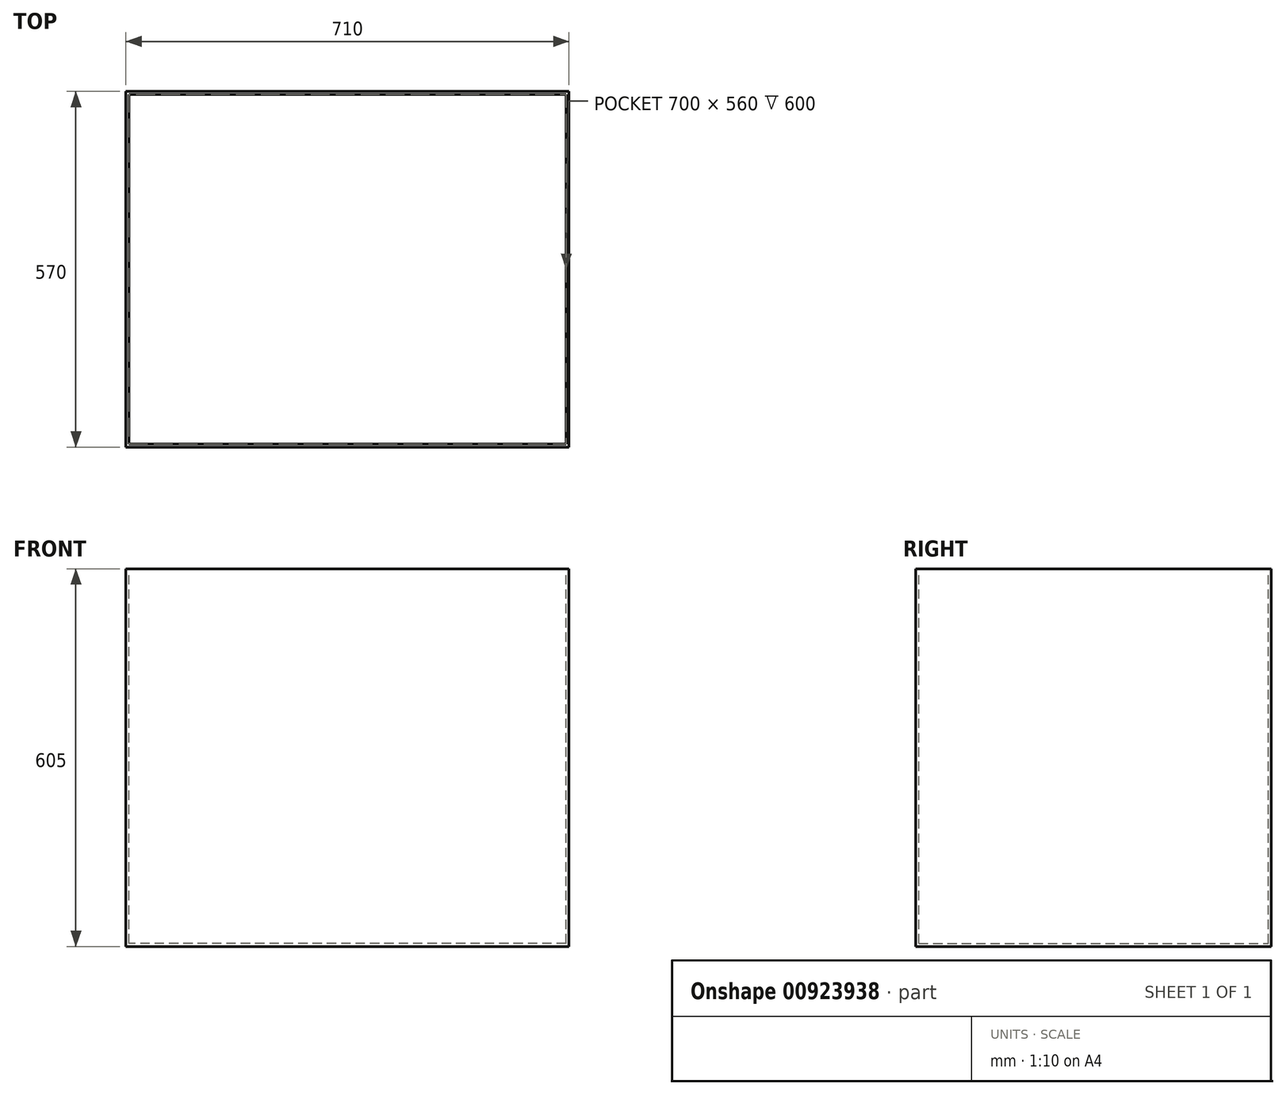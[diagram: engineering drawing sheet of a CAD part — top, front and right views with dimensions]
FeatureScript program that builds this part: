
annotation { "Feature Type Name" : "Feature", "Feature Type Description" : "" }
export const myFeature = defineFeature(function(context is Context, id is Id, definition is map)
    precondition{}
    {
        {
            var Q0;
            Q0=qCreatedBy(makeId("Top.planeOp"),FACE);
            var sketch = newSketch(context, id + "F0", { "sketchPlane" : qUnion([Q0])});
            skLineSegment(sketch, "E0.bottom", {"start": v(350, -280) * mm, "end": v(-350, -280) * mm});
            skLineSegment(sketch, "E0.top", {"start": v(350, 280) * mm, "end": v(-350, 280) * mm});
            skLineSegment(sketch, "E0.left", {"start": v(350, -280) * mm, "end": v(350, 280) * mm});
            skLineSegment(sketch, "E0.right", {"start": v(-350, -280) * mm, "end": v(-350, 280) * mm});
            skPoint(sketch, "E0.middle", {"position": v(0, 0) * mm});
            skLineSegment(sketch, "E1.bottom", {"start": v(355, -285) * mm, "end": v(-355, -285) * mm});
            skLineSegment(sketch, "E1.top", {"start": v(355, 285) * mm, "end": v(-355, 285) * mm});
            skLineSegment(sketch, "E1.left", {"start": v(355, -285) * mm, "end": v(355, 285) * mm});
            skLineSegment(sketch, "E1.right", {"start": v(-355, -285) * mm, "end": v(-355, 285) * mm});
            skSolve(sketch);
        }
        {
            var Q0;
            Q0 = qSketchRegion(id + "F0", true);
            var Q1;
            Q1=makeQuery(id+"F0.imprint","IMPRINT",FACE,{"disambiguationData":[TD([[makeQuery(id+"F0.imprint","IMPRINT",EDGE,{"derivedFrom":sQuery(id+"F0.wireOp",EDGE,"E0.bottom")}),-1.0]])]});
            extrude(context, id + "F1", {"entities" : qUnion([Q0, Q1]), "depth" : 605 * mm, "offsetDistance" : 25 * mm});
        }
        {
            var Q0;
            Q0=makeQuery(id+"F1.opExtrude","CAP_FACE",FACE,{"disambiguationData":[OSD([sQuery(id+"F0.wireOp",EDGE,"E1.bottom"),sQuery(id+"F0.wireOp",EDGE,"E1.top"),sQuery(id+"F0.wireOp",EDGE,"E1.left"),sQuery(id+"F0.wireOp",EDGE,"E1.right")])],"isStart":false});
            var sketch = newSketch(context, id + "F2", { "sketchPlane" : qUnion([Q0])});
            skLineSegment(sketch, "E2.bottom", {"start": v(350, -280) * mm, "end": v(-350, -280) * mm});
            skLineSegment(sketch, "E2.top", {"start": v(350, 280) * mm, "end": v(-350, 280) * mm});
            skLineSegment(sketch, "E2.left", {"start": v(350, -280) * mm, "end": v(350, 280) * mm});
            skLineSegment(sketch, "E2.right", {"start": v(-350, -280) * mm, "end": v(-350, 280) * mm});
            skPoint(sketch, "E2.middle", {"position": v(0, 0) * mm});
            skLineSegment(sketch, "E3.bottom", {"start": v(355, -285) * mm, "end": v(-355, -285) * mm});
            skLineSegment(sketch, "E3.top", {"start": v(355, 285) * mm, "end": v(-355, 285) * mm});
            skLineSegment(sketch, "E3.left", {"start": v(355, -285) * mm, "end": v(355, 285) * mm});
            skLineSegment(sketch, "E3.right", {"start": v(-355, -285) * mm, "end": v(-355, 285) * mm});
            skSolve(sketch);
        }
        {
            var Q0;
            Q0=makeQuery(id+"F2.imprint","IMPRINT",FACE,{"disambiguationData":[TD([[makeQuery(id+"F2.imprint","IMPRINT",EDGE,{"derivedFrom":sQuery(id+"F2.wireOp",EDGE,"E2.bottom")}),-1.0]])]});
            extrude(context, id + "F3", {"entities" : qUnion([Q0]), "operationType" : NewBodyOperationType.REMOVE, "oppositeDirection" : true, "depth" : 600 * mm, "offsetDistance" : 25 * mm});
        }
    });
